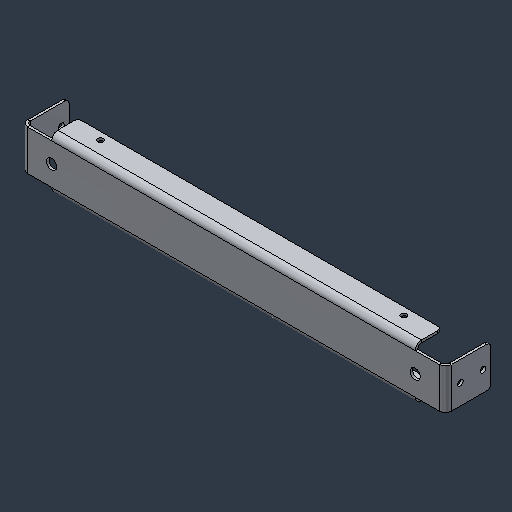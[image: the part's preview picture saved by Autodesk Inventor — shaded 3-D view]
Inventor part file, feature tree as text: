
AUTODESK INVENTOR PART (.ipt)
format: ipt  version: 2024.3 (Build 283343000, 343)  size: 124,416 bytes
history: native  units: mm (DEFAULTED — no unit token found)
features: fillet x1
ambient origin geometry x8: Origin, YZ Plane, XZ Plane, XY Plane, X Axis, Y Axis, Z Axis, Center Point
bodies: Solid1 (feature_tree)
feature tree (1):
  fillet  "Fillet1"  [1 undecoded]
note: 1 required parameter value undecoded (feature->parameter linkage not recoverable at this tier; creation-order binding heuristic only, values carry confidence <= 0.55)
